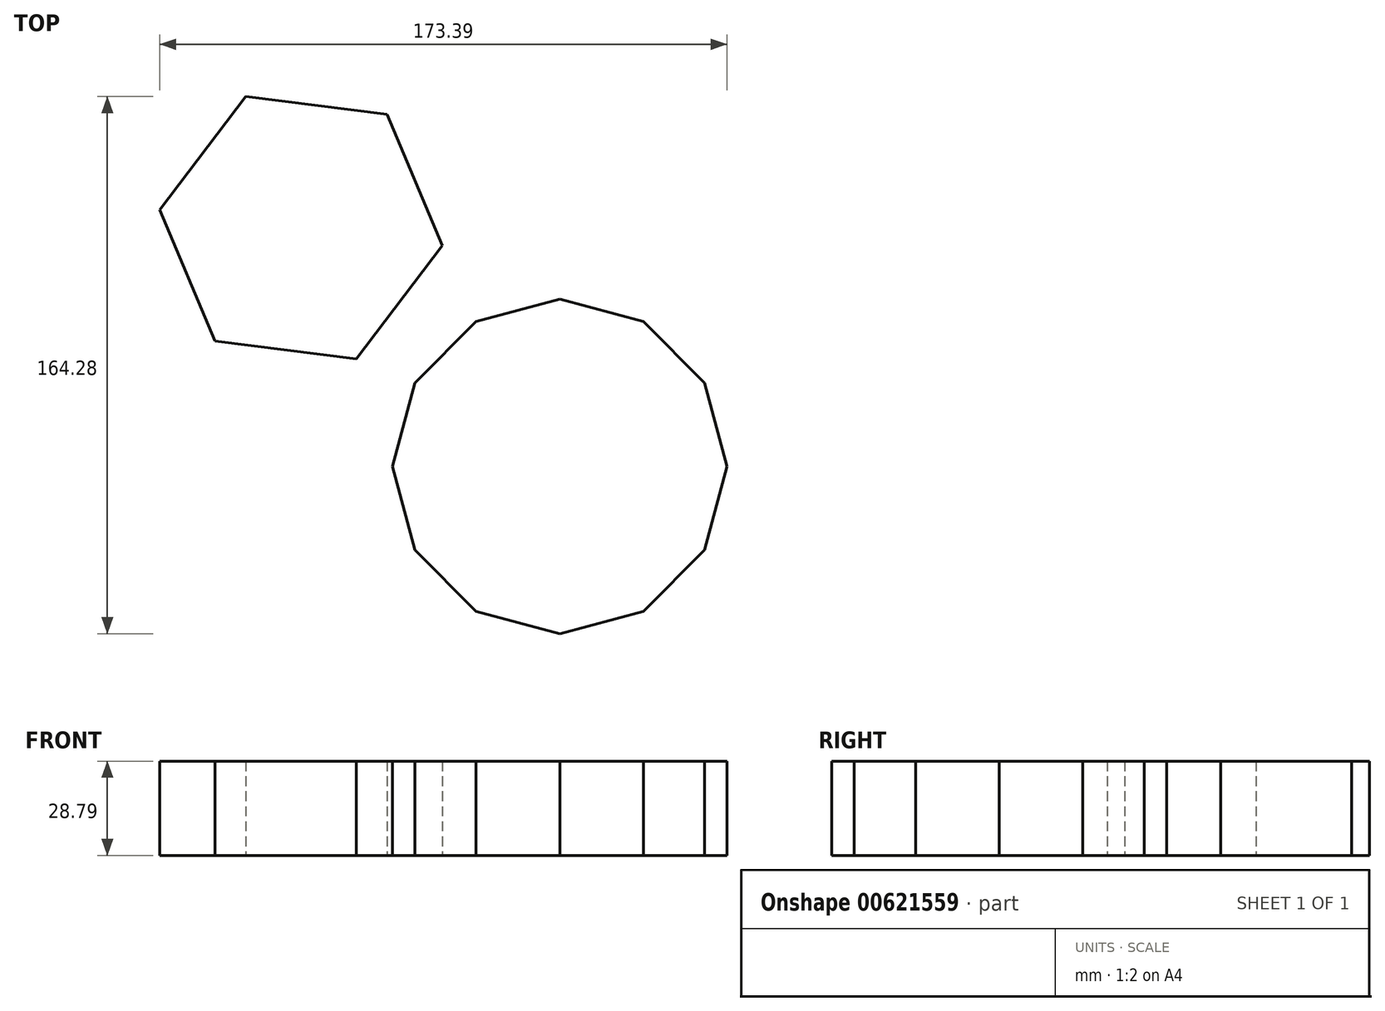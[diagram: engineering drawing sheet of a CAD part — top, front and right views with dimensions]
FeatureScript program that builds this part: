
annotation { "Feature Type Name" : "Feature", "Feature Type Description" : "" }
export const myFeature = defineFeature(function(context is Context, id is Id, definition is map)
    precondition{}
    {
        {
            var Q0;
            Q0=qCreatedBy(makeId("Top.planeOp"),FACE);
            var sketch = newSketch(context, id + "F0", { "sketchPlane" : qUnion([Q0])});
            skCircle(sketch, "E0.cCircle", {"center": v(35.92, 0) * mm, "radius": 51.15 * mm, "construction": true});
            skLineSegment(sketch, "E0.0", {"start": v(-15.23, 0) * mm, "end": v(-8.37, 25.58) * mm});
            skLineSegment(sketch, "E0.1", {"start": v(-8.37, 25.58) * mm, "end": v(10.35, 44.3) * mm});
            skLineSegment(sketch, "E0.2", {"start": v(10.35, 44.3) * mm, "end": v(35.92, 51.15) * mm});
            skLineSegment(sketch, "E0.3", {"start": v(35.92, 51.15) * mm, "end": v(61.5, 44.3) * mm});
            skLineSegment(sketch, "E0.4", {"start": v(61.5, 44.3) * mm, "end": v(80.22, 25.58) * mm});
            skLineSegment(sketch, "E0.5", {"start": v(80.22, 25.58) * mm, "end": v(87.07, 0) * mm});
            skLineSegment(sketch, "E0.6", {"start": v(87.07, 0) * mm, "end": v(80.22, -25.58) * mm});
            skLineSegment(sketch, "E0.7", {"start": v(80.22, -25.58) * mm, "end": v(61.5, -44.3) * mm});
            skLineSegment(sketch, "E0.8", {"start": v(61.5, -44.3) * mm, "end": v(35.92, -51.15) * mm});
            skLineSegment(sketch, "E0.9", {"start": v(35.92, -51.15) * mm, "end": v(10.35, -44.3) * mm});
            skLineSegment(sketch, "E0.10", {"start": v(10.35, -44.3) * mm, "end": v(-8.37, -25.58) * mm});
            skLineSegment(sketch, "E0.11", {"start": v(-8.37, -25.58) * mm, "end": v(-15.23, 0) * mm});
            skCircle(sketch, "E1.cCircle", {"center": v(-43.16, 73.04) * mm, "radius": 43.5 * mm, "construction": true});
            skLineSegment(sketch, "E1.0", {"start": v(0, 67.62) * mm, "end": v(-26.28, 32.96) * mm});
            skLineSegment(sketch, "E1.1", {"start": v(-26.28, 32.96) * mm, "end": v(-69.44, 38.38) * mm});
            skLineSegment(sketch, "E1.2", {"start": v(-69.44, 38.38) * mm, "end": v(-86.32, 78.47) * mm});
            skLineSegment(sketch, "E1.3", {"start": v(-86.32, 78.47) * mm, "end": v(-60.04, 113.13) * mm});
            skLineSegment(sketch, "E1.4", {"start": v(-60.04, 113.13) * mm, "end": v(-16.88, 107.71) * mm});
            skLineSegment(sketch, "E1.5", {"start": v(-16.88, 107.71) * mm, "end": v(0, 67.62) * mm});
            skSolve(sketch);
        }
        {
            var Q0;
            Q0 = qSketchRegion(id + "F0", true);
            extrude(context, id + "F1", {"entities" : qUnion([Q0]), "depth" : 28.8 * mm, "offsetDistance" : 25 * mm});
        }
    });
